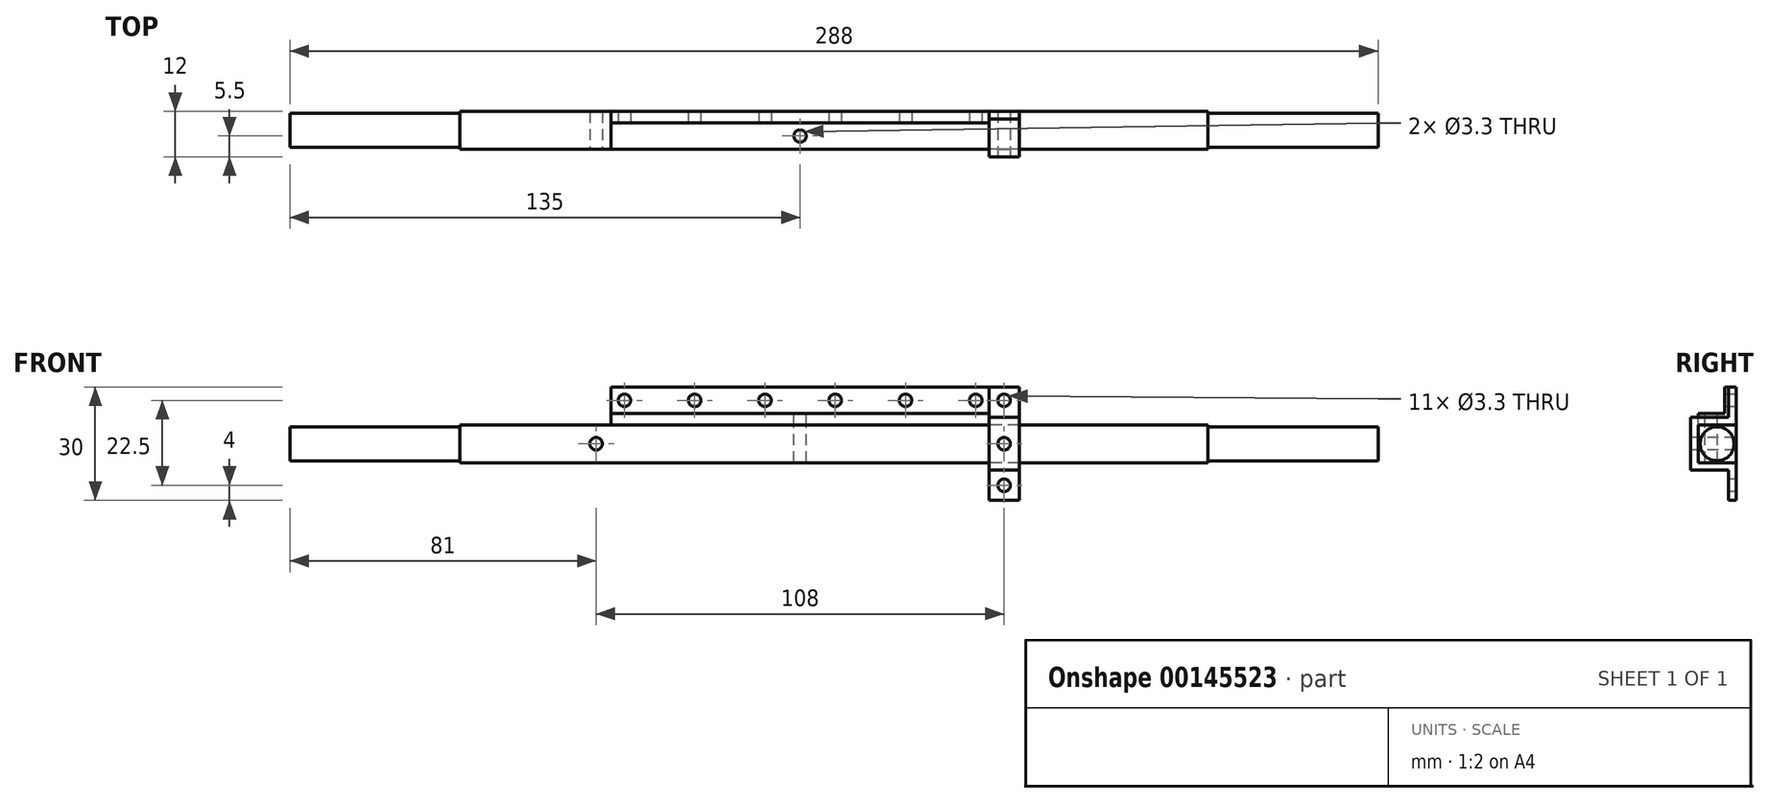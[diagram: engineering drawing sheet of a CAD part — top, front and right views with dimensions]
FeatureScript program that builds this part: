
annotation { "Feature Type Name" : "Feature", "Feature Type Description" : "" }
export const myFeature = defineFeature(function(context is Context, id is Id, definition is map)
    precondition{}
    {
        {
            var Q0;
            Q0=qCreatedBy(makeId("Right.planeOp"),FACE);
            var sketch = newSketch(context, id + "F0", { "sketchPlane" : qUnion([Q0])});
            skLineSegment(sketch, "E0.top", {"start": v(0, 10) * mm, "end": v(-3, 10) * mm});
            skLineSegment(sketch, "E0.left", {"start": v(0, 0) * mm, "end": v(0, 10) * mm});
            skLineSegment(sketch, "E0.right", {"start": v(-3, 3) * mm, "end": v(-3, 10) * mm});
            skLineSegment(sketch, "E1.top", {"start": v(-3, 3) * mm, "end": v(-10, 3) * mm});
            skLineSegment(sketch, "E1.right", {"start": v(-10, 0) * mm, "end": v(-10, 3) * mm});
            skLineSegment(sketch, "E2", {"start": v(-10, 0) * mm, "end": v(0, 0) * mm});
            skSolve(sketch);
        }
        {
            var Q0;
            Q0=makeQuery(id+"F0.imprint","IMPRINT",FACE,{"disambiguationData":[TD([[makeQuery(id+"F0.imprint","IMPRINT",EDGE,{"derivedFrom":sQuery(id+"F0.wireOp",EDGE,"E0.top")}),1.0]])]});
            extrude(context, id + "F1", {"entities" : qUnion([Q0]), "depth" : 50 * mm, "hasSecondDirection" : true, "secondDirectionOppositeDirection" : true, "secondDirectionDepth" : 50 * mm});
        }
        {
            var Q0;
            Q0=qCreatedBy(makeId("Right.planeOp"),FACE);
            var sketch = newSketch(context, id + "F2", { "sketchPlane" : qUnion([Q0])});
            skLineSegment(sketch, "E3.bottom", {"start": v(0, 0) * mm, "end": v(-10, 0) * mm});
            skLineSegment(sketch, "E3.top", {"start": v(0, -10) * mm, "end": v(-10, -10) * mm});
            skLineSegment(sketch, "E3.left", {"start": v(0, 0) * mm, "end": v(0, -10) * mm});
            skLineSegment(sketch, "E3.right", {"start": v(-10, 0) * mm, "end": v(-10, -10) * mm});
            skSolve(sketch);
        }
        {
            var Q0;
            Q0=qSketchRegion(id+"F2",true);
            extrude(context, id + "F3", {"entities" : qUnion([Q0]), "depth" : 108 * mm, "hasSecondDirection" : true, "secondDirectionOppositeDirection" : true, "secondDirectionDepth" : 90 * mm});
        }
        {
            var Q0;
            Q0=makeQuery(id+"F3.opExtrude","CAP_FACE",FACE,{"disambiguationData":[OSD([sQuery(id+"F2.wireOp",EDGE,"E3.bottom"),sQuery(id+"F2.wireOp",EDGE,"E3.top"),sQuery(id+"F2.wireOp",EDGE,"E3.left"),sQuery(id+"F2.wireOp",EDGE,"E3.right")])],"isStart":false});
            var sketch = newSketch(context, id + "F4", { "sketchPlane" : qUnion([Q0])});
            skCircle(sketch, "E4", {"center": v(-5, -5) * mm, "radius": 4.5 * mm});
            skPoint(sketch, "E4.centerSnap0", {"position": v(-5, 0) * mm});
            skPoint(sketch, "E4.centerSnap1", {"position": v(0, -5) * mm});
            skSolve(sketch);
        }
        {
            var Q0;
            Q0=qSketchRegion(id+"F4",true);
            extrude(context, id + "F5", {"entities" : qUnion([Q0]), "operationType" : NewBodyOperationType.ADD, "depth" : 45 * mm});
        }
        {
            var Q0;
            Q0=makeQuery(id+"F3.opExtrude","CAP_FACE",FACE,{"disambiguationData":[OSD([sQuery(id+"F2.wireOp",EDGE,"E3.bottom"),sQuery(id+"F2.wireOp",EDGE,"E3.top"),sQuery(id+"F2.wireOp",EDGE,"E3.left"),sQuery(id+"F2.wireOp",EDGE,"E3.right")])],"isStart":true});
            var sketch = newSketch(context, id + "F6", { "sketchPlane" : qUnion([Q0])});
            skCircle(sketch, "E5", {"center": v(5, -5) * mm, "radius": 4.5 * mm});
            skPoint(sketch, "E5.centerSnap0", {"position": v(10, -5) * mm});
            skPoint(sketch, "E5.centerSnap1", {"position": v(5, 0) * mm});
            skSolve(sketch);
        }
        {
            var Q0;
            Q0=makeQuery(id+"F6.imprint","IMPRINT",FACE,{"disambiguationData":[TD([[makeQuery(id+"F6.imprint","IMPRINT",EDGE,{"derivedFrom":sQuery(id+"F6.wireOp",EDGE,"E5")}),1.0]])]});
            extrude(context, id + "F7", {"entities" : qUnion([Q0]), "operationType" : NewBodyOperationType.ADD, "depth" : 45 * mm});
        }
        {
            var Q0;
            Q0=qCreatedBy(makeId("Right.planeOp"),FACE);
            var sketch = newSketch(context, id + "F8", { "sketchPlane" : qUnion([Q0])});
            skLineSegment(sketch, "E6", {"start": v(0, 10) * mm, "end": v(0, 0) * mm});
            skLineSegment(sketch, "E7", {"start": v(0, 0) * mm, "end": v(-10, 0) * mm});
            skLineSegment(sketch, "E8", {"start": v(-10, 0) * mm, "end": v(-10, -5) * mm});
            skLineSegment(sketch, "E9", {"start": v(-12, -5) * mm, "end": v(-12, 2) * mm});
            skLineSegment(sketch, "E10", {"start": v(-12, 2) * mm, "end": v(-2, 2) * mm});
            skLineSegment(sketch, "E11", {"start": v(-2, 2) * mm, "end": v(-2, 10) * mm});
            skLineSegment(sketch, "E12", {"start": v(-2, 10) * mm, "end": v(0, 10) * mm});
            skLineSegment(sketch, "E13", {"start": v(-4.92, 2) * mm, "end": v(-4.92, 0) * mm, "construction": true});
            skLineSegment(sketch, "E14", {"start": v(-10, -5) * mm, "end": v(-3.24, -5) * mm, "construction": true});
            skLineSegment(sketch, "E15", {"start": v(-12, -2.81) * mm, "end": v(-10, -2.81) * mm, "construction": true});
            skLineSegment(sketch, "E16.MirrorCS", {"start": v(-10, -10) * mm, "end": v(-10, -5) * mm});
            skLineSegment(sketch, "E17.MirrorCS", {"start": v(-2, -12) * mm, "end": v(-2, -20) * mm});
            skLineSegment(sketch, "E18.MirrorCS", {"start": v(-12, -12) * mm, "end": v(-2, -12) * mm});
            skLineSegment(sketch, "E19.MirrorCS", {"start": v(-12, -5) * mm, "end": v(-12, -12) * mm});
            skLineSegment(sketch, "E20.MirrorCS", {"start": v(-2, -20) * mm, "end": v(0, -20) * mm});
            skLineSegment(sketch, "E21.MirrorCS", {"start": v(0, -10) * mm, "end": v(-10, -10) * mm});
            skLineSegment(sketch, "E22.MirrorCS", {"start": v(0, -20) * mm, "end": v(0, -10) * mm});
            skSolve(sketch);
        }
        {
            var Q0;
            Q0=qSketchRegion(id+"F8",true);
            extrude(context, id + "F9", {"entities" : qUnion([Q0]), "depth" : 8 * mm});
        }
        {
            var Q0;
            Q0=makeQuery(id+"F9.opExtrude","SWEPT_BODY",BODY,{"disambiguationData":[OSD([sQuery(id+"F8.wireOp",EDGE,"E6"),sQuery(id+"F8.wireOp",EDGE,"E7"),sQuery(id+"F8.wireOp",EDGE,"E8"),sQuery(id+"F8.wireOp",EDGE,"E9"),sQuery(id+"F8.wireOp",EDGE,"E10"),sQuery(id+"F8.wireOp",EDGE,"E11"),sQuery(id+"F8.wireOp",EDGE,"E12"),sQuery(id+"F8.wireOp",EDGE,"E16.MirrorCS"),sQuery(id+"F8.wireOp",EDGE,"E17.MirrorCS"),sQuery(id+"F8.wireOp",EDGE,"E18.MirrorCS"),sQuery(id+"F8.wireOp",EDGE,"E19.MirrorCS"),sQuery(id+"F8.wireOp",EDGE,"E20.MirrorCS"),sQuery(id+"F8.wireOp",EDGE,"E21.MirrorCS"),sQuery(id+"F8.wireOp",EDGE,"E22.MirrorCS")])]});
            transform(context, id + "F10", {"entities" : qUnion([Q0]), "transformType" : TransformType.TRANSLATION_3D, "dx" : 50 * mm, "dy" : 0 * mm, "dz" : 0 * mm, "makeCopy" : false});
        }
        {
            var Q0;
            Q0=makeQuery(id+"F9.opExtrude","SWEPT_FACE",FACE,{"disambiguationData":[OSD([sQuery(id+"F8.wireOp",EDGE,"E9"),sQuery(id+"F8.wireOp",EDGE,"E19.MirrorCS")])]});
            var sketch = newSketch(context, id + "F11", { "sketchPlane" : qUnion([Q0])});
            skLineSegment(sketch, "E23", {"start": v(-46.5, 6.5) * mm, "end": v(-27.9, 6.5) * mm, "construction": true});
            skLineSegment(sketch, "E24", {"start": v(-27.9, 6.5) * mm, "end": v(-9.3, 6.5) * mm, "construction": true});
            skLineSegment(sketch, "E25", {"start": v(-9.3, 6.5) * mm, "end": v(9.3, 6.5) * mm, "construction": true});
            skLineSegment(sketch, "E26", {"start": v(9.3, 6.5) * mm, "end": v(27.9, 6.5) * mm, "construction": true});
            skLineSegment(sketch, "E27", {"start": v(27.9, 6.5) * mm, "end": v(46.5, 6.5) * mm, "construction": true});
            skLineSegment(sketch, "E28", {"start": v(46.5, 6.5) * mm, "end": v(54, 6.5) * mm, "construction": true});
            skLineSegment(sketch, "E29", {"start": v(54, 6.5) * mm, "end": v(54, -5) * mm, "construction": true});
            skLineSegment(sketch, "E30", {"start": v(54, -5) * mm, "end": v(54, -16) * mm, "construction": true});
            skLineSegment(sketch, "E31", {"start": v(54, -5) * mm, "end": v(60.6, -5) * mm, "construction": true});
            skLineSegment(sketch, "E32", {"start": v(54, -16) * mm, "end": v(60.3, -16) * mm, "construction": true});
            skLineSegment(sketch, "E33", {"start": v(0, 10) * mm, "end": v(0, 2.91) * mm, "construction": true});
            skLineSegment(sketch, "E34", {"start": v(-46.5, 10) * mm, "end": v(-46.5, 6.5) * mm, "construction": true});
            skLineSegment(sketch, "E35", {"start": v(-46.5, 6.5) * mm, "end": v(-50, 6.5) * mm, "construction": true});
            skLineSegment(sketch, "E36.MirrorCS", {"start": v(-54, -5) * mm, "end": v(-60.6, -5) * mm, "construction": true});
            skSolve(sketch);
        }
        {
            var Q0;
            Q0=makeQuery(id+"F1.opExtrude","SWEPT_FACE",FACE,{"disambiguationData":[OSD([sQuery(id+"F0.wireOp",EDGE,"E1.top")])]});
            var sketch = newSketch(context, id + "F12", { "sketchPlane" : qUnion([Q0])});
            skLineSegment(sketch, "E37", {"start": v(50, -6.5) * mm, "end": v(0, -6.5) * mm, "construction": true});
            skPoint(sketch, "E37.endSnap0", {"position": v(0, -10) * mm});
            skLineSegment(sketch, "E38", {"start": v(0, -6.5) * mm, "end": v(0, -10) * mm, "construction": true});
            skSolve(sketch);
        }
        {
            var Q0;
            Q0=sQuery(id+"F11.wireOp",VERTEX,"E34.end");
            var Q1;
            Q1=sQuery(id+"F11.wireOp",VERTEX,"E24.start");
            var Q2;
            Q2=sQuery(id+"F11.wireOp",VERTEX,"E25.start");
            var Q3;
            Q3=sQuery(id+"F11.wireOp",VERTEX,"E26.start");
            var Q4;
            Q4=sQuery(id+"F11.wireOp",VERTEX,"E27.start");
            var Q5;
            Q5=sQuery(id+"F11.wireOp",VERTEX,"E28.start");
            var Q6;
            Q6=sQuery(id+"F11.wireOp",VERTEX,"E29.start");
            var Q7;
            Q7=sQuery(id+"F11.wireOp",VERTEX,"E31.start");
            var Q8;
            Q8=sQuery(id+"F11.wireOp",VERTEX,"E32.start");
            var Q9;
            Q9=sQuery(id+"F11.wireOp",VERTEX,"E36.MirrorCS.start");
            var Q10;
            Q10=sQuery(id+"F12.wireOp",VERTEX,"E38.start");
            var Q11;
            Q11=makeQuery(id+"F9.opExtrude","SWEPT_BODY",BODY,{"disambiguationData":[OSD([sQuery(id+"F8.wireOp",EDGE,"E6"),sQuery(id+"F8.wireOp",EDGE,"E7"),sQuery(id+"F8.wireOp",EDGE,"E8"),sQuery(id+"F8.wireOp",EDGE,"E9"),sQuery(id+"F8.wireOp",EDGE,"E10"),sQuery(id+"F8.wireOp",EDGE,"E11"),sQuery(id+"F8.wireOp",EDGE,"E12"),sQuery(id+"F8.wireOp",EDGE,"E16.MirrorCS"),sQuery(id+"F8.wireOp",EDGE,"E17.MirrorCS"),sQuery(id+"F8.wireOp",EDGE,"E18.MirrorCS"),sQuery(id+"F8.wireOp",EDGE,"E19.MirrorCS"),sQuery(id+"F8.wireOp",EDGE,"E20.MirrorCS"),sQuery(id+"F8.wireOp",EDGE,"E21.MirrorCS"),sQuery(id+"F8.wireOp",EDGE,"E22.MirrorCS")])]});
            var Q12;
            Q12=makeQuery(id+"F3.opExtrude","SWEPT_BODY",BODY,{"disambiguationData":[OSD([sQuery(id+"F2.wireOp",EDGE,"E3.bottom"),sQuery(id+"F2.wireOp",EDGE,"E3.top"),sQuery(id+"F2.wireOp",EDGE,"E3.left"),sQuery(id+"F2.wireOp",EDGE,"E3.right")])]});
            var Q13;
            Q13=makeQuery(id+"F1.opExtrude","SWEPT_BODY",BODY,{"disambiguationData":[OSD([sQuery(id+"F0.wireOp",EDGE,"E0.top"),sQuery(id+"F0.wireOp",EDGE,"E0.left"),sQuery(id+"F0.wireOp",EDGE,"E0.right"),sQuery(id+"F0.wireOp",EDGE,"E1.top"),sQuery(id+"F0.wireOp",EDGE,"E1.right"),sQuery(id+"F0.wireOp",EDGE,"E2")])]});
            hole(context, id + "F13", {"style" : HoleStyle.SIMPLE, "endStyle" : HoleEndStyle.THROUGH, "standardTappedOrClearance" : lookupTablePath({ "standard" : "ISO", "fit" : "Normal", "size" : "M3", "type" : "Clearance" }), "standardBlindInLast" : lookupTablePath({ "fit" : "Standard", "standard" : "ISO", "size" : "M3", "type" : "Clearance" }), "holeDiameter" : 3.3 * mm, "startFromSketch" : true, "locations" : qUnion([Q0, Q1, Q2, Q3, Q4, Q5, Q6, Q7, Q8, Q9, Q10]), "scope" : qUnion([Q11, Q12, Q13]), "isTappedThrough" : true});
        }
    });
